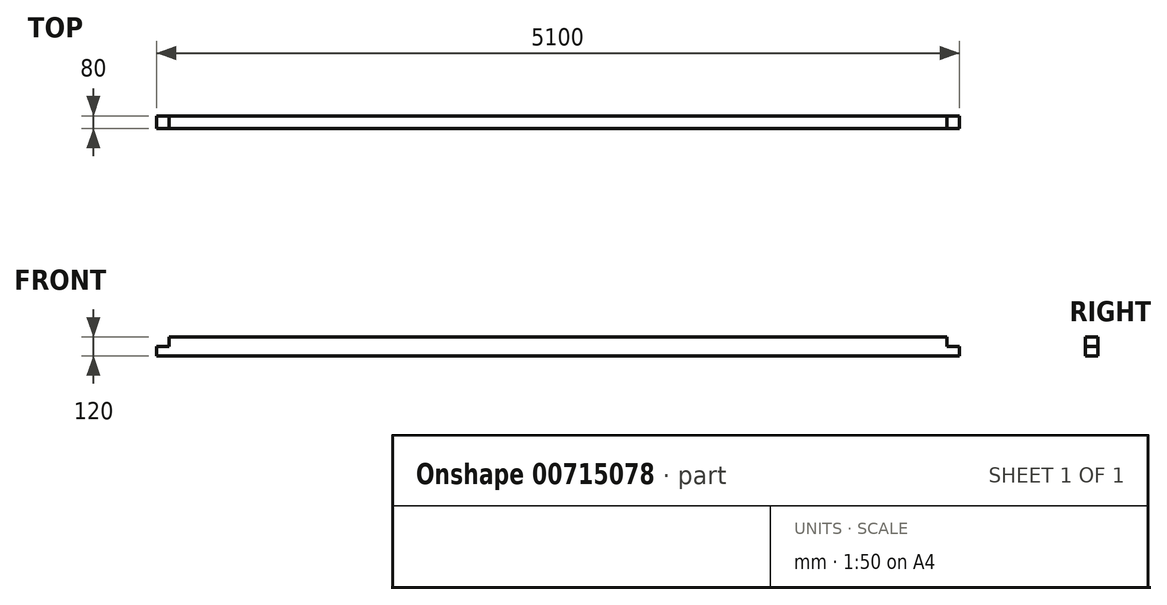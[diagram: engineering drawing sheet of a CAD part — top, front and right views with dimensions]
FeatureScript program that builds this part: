
annotation { "Feature Type Name" : "Feature", "Feature Type Description" : "" }
export const myFeature = defineFeature(function(context is Context, id is Id, definition is map)
    precondition{}
    {
        {
            var Q0;
            Q0=qCreatedBy(makeId("Right.planeOp"),FACE);
            var sketch = newSketch(context, id + "F0", { "sketchPlane" : qUnion([Q0])});
            skLineSegment(sketch, "E0.bottom", {"start": v(-40, 60) * mm, "end": v(40, 60) * mm});
            skLineSegment(sketch, "E0.top", {"start": v(-40, -60) * mm, "end": v(40, -60) * mm});
            skLineSegment(sketch, "E0.left", {"start": v(-40, 60) * mm, "end": v(-40, -60) * mm});
            skLineSegment(sketch, "E0.right", {"start": v(40, 60) * mm, "end": v(40, -60) * mm});
            skPoint(sketch, "E0.middle", {"position": v(0, 0) * mm});
            skSolve(sketch);
        }
        {
            var Q0;
            Q0=makeQuery(id+"F0.imprint","IMPRINT",FACE,{"disambiguationData":[TD([[makeQuery(id+"F0.imprint","IMPRINT",EDGE,{"derivedFrom":sQuery(id+"F0.wireOp",EDGE,"E0.bottom")}),-1.0]])]});
            extrude(context, id + "F1", {"entities" : qUnion([Q0]), "depth" : 5100 * mm, "offsetDistance" : 25 * mm});
        }
        {
            var Q0;
            Q0=makeQuery(id+"F1.opExtrude","SWEPT_FACE",FACE,{"disambiguationData":[OSD([sQuery(id+"F0.wireOp",EDGE,"E0.left")])]});
            var sketch = newSketch(context, id + "F2", { "sketchPlane" : qUnion([Q0])});
            skLineSegment(sketch, "E1.bottom", {"start": v(-80, 0) * mm, "end": v(80, 0) * mm});
            skLineSegment(sketch, "E1.top", {"start": v(-80, 120) * mm, "end": v(80, 120) * mm});
            skLineSegment(sketch, "E1.left", {"start": v(-80, 0) * mm, "end": v(-80, 120) * mm});
            skLineSegment(sketch, "E1.right", {"start": v(80, 0) * mm, "end": v(80, 120) * mm});
            skPoint(sketch, "E1.middle", {"position": v(0, 60) * mm});
            skPoint(sketch, "E1.cornerSnap0", {"position": v(0, 0) * mm});
            skLineSegment(sketch, "E2.bottom", {"start": v(5180, 0) * mm, "end": v(5020, 0) * mm});
            skLineSegment(sketch, "E2.top", {"start": v(5180, 120) * mm, "end": v(5020, 120) * mm});
            skLineSegment(sketch, "E2.left", {"start": v(5180, 0) * mm, "end": v(5180, 120) * mm});
            skLineSegment(sketch, "E2.right", {"start": v(5020, 0) * mm, "end": v(5020, 120) * mm});
            skPoint(sketch, "E2.middle", {"position": v(5100, 60) * mm});
            skSolve(sketch);
        }
        {
            var Q0;
            {var subQ0=sQuery(id+"F2.wireOp",EDGE,"E2.right");var subQ1=sQuery(id+"F2.wireOp",EDGE,"E2.bottom");var subQ2=makeQuery(id+"F2.imprint","INTERSECT",VERTEX,{"derivedFrom":[subQ1,subQ0]});Q0=makeQuery(id+"F2.imprint","IMPRINT",FACE,{"disambiguationData":[TD([[makeQuery(id+"F2.imprint","IMPRINT",EDGE,{"disambiguationData":[TD([[subQ2,1.0]])],"derivedFrom":subQ1}),-1.0]])]});}
            var Q1;
            {var subQ0=sQuery(id+"F2.wireOp",EDGE,"E1.right");var subQ1=sQuery(id+"F2.wireOp",EDGE,"E1.bottom");var subQ2=makeQuery(id+"F2.imprint","INTERSECT",VERTEX,{"derivedFrom":[subQ1,subQ0]});Q1=makeQuery(id+"F2.imprint","IMPRINT",FACE,{"disambiguationData":[TD([[makeQuery(id+"F2.imprint","IMPRINT",EDGE,{"disambiguationData":[TD([[subQ2,1.0]])],"derivedFrom":subQ1}),1.0]])]});}
            extrude(context, id + "F3", {"entities" : qUnion([Q0, Q1]), "operationType" : NewBodyOperationType.REMOVE, "endBound" : BoundingType.UP_TO_NEXT, "oppositeDirection" : true, "depth" : 25 * mm, "offsetDistance" : 25 * mm});
        }
    });
